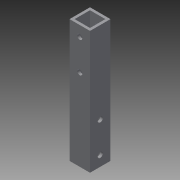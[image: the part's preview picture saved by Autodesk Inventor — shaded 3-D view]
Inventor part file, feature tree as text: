
AUTODESK INVENTOR PART (.ipt)
format: ipt  version: 2013 (Build 170138000, 138)  size: 108,544 bytes
history: native  units: in
note: dims shown in document units (in); Inventor stores cm internally (conversion verified against a paired STEP export)
features: extrude x3, sketch x3
ambient origin geometry x8: Origin, YZ Plane, XZ Plane, XY Plane, X Axis, Y Axis, Z Axis, Center Point
bodies: Solid1 (feature_tree)
feature tree (6):
  extrude  "Extrusion1"  Depth=1.0in
  extrude  "Extrusion2"  Depth=0.75in
  extrude  "Extrusion3"  Depth=0.5in
  sketch  "Sketch1"  dims[d0=1.0in d1=1.0in]
  sketch  "Sketch2"  dims[d2=0.75in d3=0.75in]
  sketch  "Sketch3"  dims[d4=6.0in d5=0.0in d6=0.5in d7=1.5in d8=180.0deg d9=0.25in d10=0.25in d11=1.0in d12=0.0in d13=0.5in d14=90.0deg d15=1.5in d16=90.0deg d17=0.25in d18=0.25in d19=1.0in d20=0.0in]
